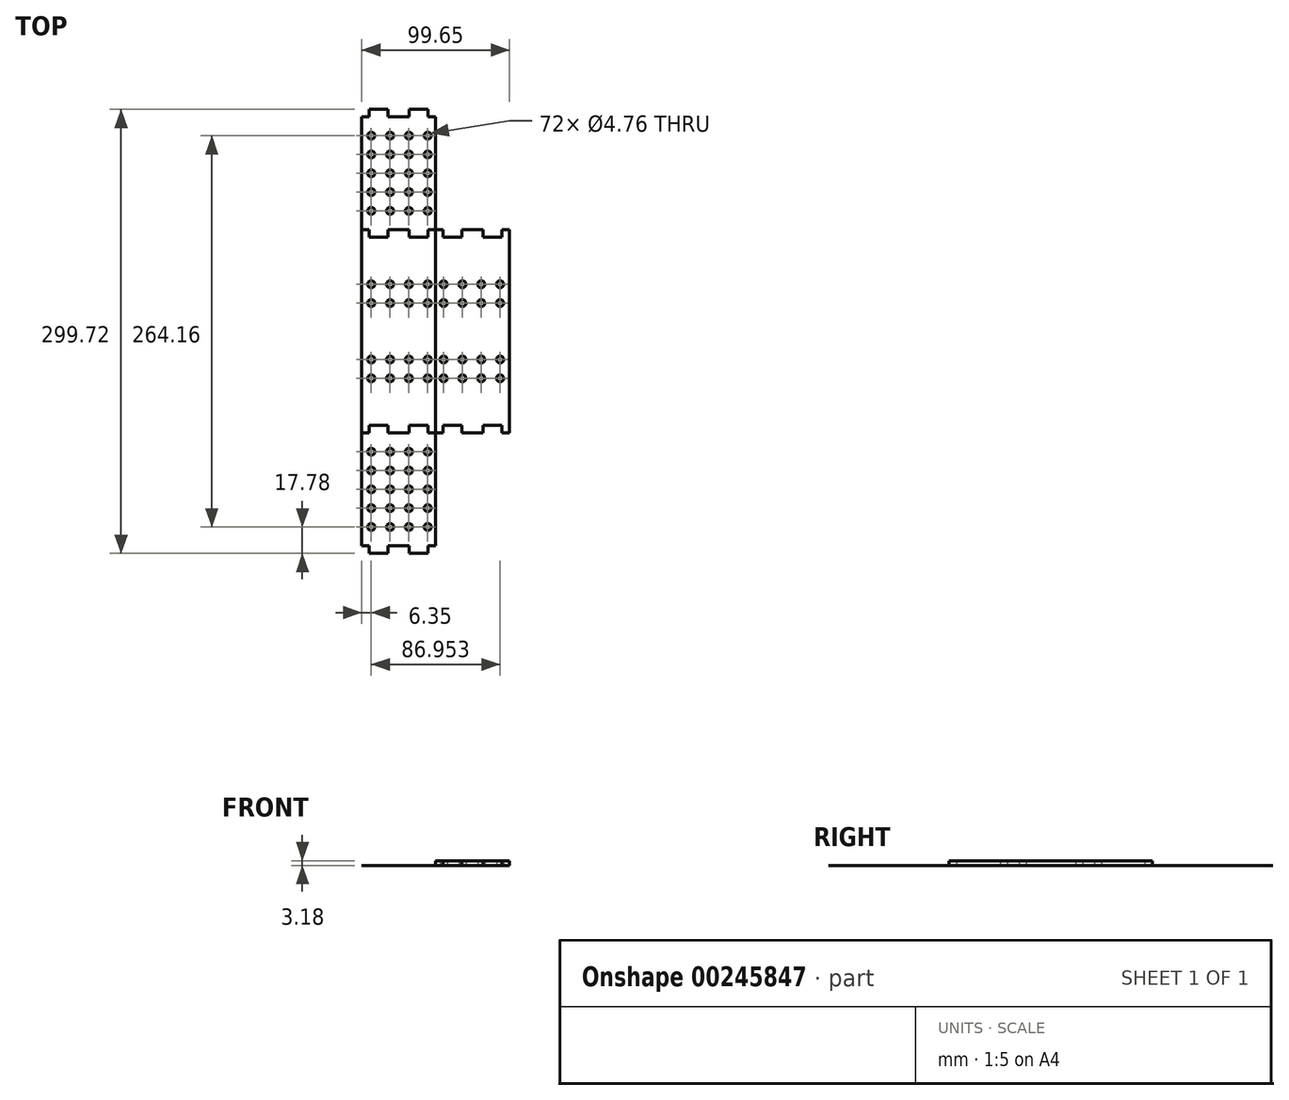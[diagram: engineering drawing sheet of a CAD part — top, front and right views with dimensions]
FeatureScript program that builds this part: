
annotation { "Feature Type Name" : "Feature", "Feature Type Description" : "" }
export const myFeature = defineFeature(function(context is Context, id is Id, definition is map)
    precondition{}
    {
        {
            var Q0;
            Q0=qCreatedBy(makeId("Top.planeOp"),FACE);
            var sketch = newSketch(context, id + "F0", { "sketchPlane" : qUnion([Q0])});
            skLineSegment(sketch, "E0.bottom", {"start": v(-123.2, 27.94) * mm, "end": v(-123.19, 27.94) * mm});
            skLineSegment(sketch, "E0.top", {"start": v(-123.19, -27.94) * mm, "end": v(-123.19, -27.94) * mm});
            skCircle(sketch, "E1.1.0.0", {"center": v(-25.4, -31.75) * mm, "radius": 2.38 * mm});
            skCircle(sketch, "E1.1.1.0", {"center": v(-25.4, -19.05) * mm, "radius": 2.38 * mm});
            skCircle(sketch, "E1.2.0.0", {"center": v(-12.7, -31.75) * mm, "radius": 2.38 * mm});
            skCircle(sketch, "E1.2.1.0", {"center": v(-12.7, -19.05) * mm, "radius": 2.38 * mm});
            skCircle(sketch, "E1.3.0.0", {"center": v(0, -31.75) * mm, "radius": 2.38 * mm});
            skCircle(sketch, "E1.3.1.0", {"center": v(0, -19.05) * mm, "radius": 2.38 * mm});
            skCircle(sketch, "E1.4.0.0", {"center": v(12.7, -31.75) * mm, "radius": 2.38 * mm});
            skCircle(sketch, "E1.4.1.0", {"center": v(12.7, -19.05) * mm, "radius": 2.38 * mm});
            skCircle(sketch, "E2.MirrorC", {"center": v(-12.7, 19.05) * mm, "radius": 2.38 * mm});
            skCircle(sketch, "E3.MirrorC", {"center": v(0, 31.75) * mm, "radius": 2.38 * mm});
            skCircle(sketch, "E4.MirrorC", {"center": v(-25.4, 31.75) * mm, "radius": 2.38 * mm});
            skCircle(sketch, "E5.MirrorC", {"center": v(12.7, 19.05) * mm, "radius": 2.38 * mm});
            skCircle(sketch, "E6.MirrorC", {"center": v(0, 19.05) * mm, "radius": 2.38 * mm});
            skCircle(sketch, "E7.MirrorC", {"center": v(-25.4, 19.05) * mm, "radius": 2.38 * mm});
            skCircle(sketch, "E8.MirrorC", {"center": v(-12.7, 31.75) * mm, "radius": 2.38 * mm});
            skCircle(sketch, "E9.MirrorC", {"center": v(12.7, 31.75) * mm, "radius": 2.38 * mm});
            skLineSegment(sketch, "E10", {"start": v(-31.75, 38.1) * mm, "end": v(-31.75, -38.1) * mm});
            skPoint(sketch, "E10.startSnap0", {"position": v(-31.75, 31.75) * mm});
            skPoint(sketch, "E11.startSnap0", {"position": v(18.08, 31.75) * mm});
            skLineSegment(sketch, "E12", {"start": v(18.08, 38.1) * mm, "end": v(18.08, -38.1) * mm});
            skLineSegment(sketch, "E13.top", {"start": v(-31.75, 68.58) * mm, "end": v(-26.67, 68.58) * mm});
            skLineSegment(sketch, "E13.left", {"start": v(-31.75, 38.1) * mm, "end": v(-31.75, 68.58) * mm});
            skLineSegment(sketch, "E13.right", {"start": v(18.08, 38.1) * mm, "end": v(18.08, 68.58) * mm});
            skLineSegment(sketch, "E14", {"start": v(-26.67, 68.58) * mm, "end": v(-26.67, 63.5) * mm});
            skLineSegment(sketch, "E15", {"start": v(-26.67, 63.5) * mm, "end": v(-13.97, 63.5) * mm});
            skLineSegment(sketch, "E16", {"start": v(-13.97, 63.5) * mm, "end": v(-13.97, 68.58) * mm});
            skLineSegment(sketch, "E17", {"start": v(0.3, 68.58) * mm, "end": v(0.3, 63.5) * mm});
            skLineSegment(sketch, "E18", {"start": v(0.3, 63.5) * mm, "end": v(13, 63.5) * mm});
            skLineSegment(sketch, "E19", {"start": v(13, 63.5) * mm, "end": v(13, 68.58) * mm});
            skLineSegment(sketch, "E20.left", {"start": v(-31.75, 68.58) * mm, "end": v(-31.75, 144.78) * mm});
            skLineSegment(sketch, "E20.right", {"start": v(18.08, 68.58) * mm, "end": v(18.08, 144.78) * mm});
            skLineSegment(sketch, "E21.trimOffspring", {"start": v(-13.97, 68.58) * mm, "end": v(0.3, 68.58) * mm});
            skLineSegment(sketch, "E22.trimOffspring", {"start": v(13, 68.58) * mm, "end": v(18.08, 68.58) * mm});
            skCircle(sketch, "E23.MirrorC", {"center": v(-25.4, 81.28) * mm, "radius": 2.38 * mm});
            skCircle(sketch, "E24.0.1.0", {"center": v(-25.4, 93.98) * mm, "radius": 2.38 * mm});
            skCircle(sketch, "E24.0.2.0", {"center": v(-25.4, 106.68) * mm, "radius": 2.38 * mm});
            skCircle(sketch, "E24.0.3.0", {"center": v(-25.4, 119.38) * mm, "radius": 2.38 * mm});
            skCircle(sketch, "E24.0.4.0", {"center": v(-25.4, 132.08) * mm, "radius": 2.38 * mm});
            skCircle(sketch, "E24.1.0.0", {"center": v(-12.7, 81.28) * mm, "radius": 2.38 * mm});
            skCircle(sketch, "E24.1.1.0", {"center": v(-12.7, 93.98) * mm, "radius": 2.38 * mm});
            skCircle(sketch, "E24.1.2.0", {"center": v(-12.7, 106.68) * mm, "radius": 2.38 * mm});
            skCircle(sketch, "E24.1.3.0", {"center": v(-12.7, 119.38) * mm, "radius": 2.38 * mm});
            skCircle(sketch, "E24.1.4.0", {"center": v(-12.7, 132.08) * mm, "radius": 2.38 * mm});
            skCircle(sketch, "E24.2.0.0", {"center": v(0, 81.28) * mm, "radius": 2.38 * mm});
            skCircle(sketch, "E24.2.1.0", {"center": v(0, 93.98) * mm, "radius": 2.38 * mm});
            skCircle(sketch, "E24.2.2.0", {"center": v(0, 106.68) * mm, "radius": 2.38 * mm});
            skCircle(sketch, "E24.2.3.0", {"center": v(0, 119.38) * mm, "radius": 2.38 * mm});
            skCircle(sketch, "E24.2.4.0", {"center": v(0, 132.08) * mm, "radius": 2.38 * mm});
            skCircle(sketch, "E24.3.0.0", {"center": v(12.7, 81.28) * mm, "radius": 2.38 * mm});
            skCircle(sketch, "E24.3.1.0", {"center": v(12.7, 93.98) * mm, "radius": 2.38 * mm});
            skCircle(sketch, "E24.3.2.0", {"center": v(12.7, 106.68) * mm, "radius": 2.38 * mm});
            skCircle(sketch, "E24.3.3.0", {"center": v(12.7, 119.38) * mm, "radius": 2.38 * mm});
            skCircle(sketch, "E24.3.4.0", {"center": v(12.7, 132.08) * mm, "radius": 2.38 * mm});
            skLineSegment(sketch, "E24.direction1", {"start": v(-25.4, 81.28) * mm, "end": v(-12.7, 81.28) * mm, "construction": true});
            skLineSegment(sketch, "E24.direction2", {"start": v(-25.4, 81.28) * mm, "end": v(-25.4, 93.98) * mm, "construction": true});
            skLineSegment(sketch, "E25", {"start": v(-31.75, 0) * mm, "end": v(18.08, 0) * mm, "construction": true});
            skLineSegment(sketch, "E26.MirrorCS", {"start": v(0.3, -68.58) * mm, "end": v(0.3, -63.5) * mm});
            skCircle(sketch, "E27.MirrorC", {"center": v(0, -106.68) * mm, "radius": 2.38 * mm});
            skLineSegment(sketch, "E28.MirrorCS", {"start": v(13, -68.58) * mm, "end": v(18.08, -68.58) * mm});
            skCircle(sketch, "E29.MirrorC", {"center": v(12.7, -119.38) * mm, "radius": 2.38 * mm});
            skLineSegment(sketch, "E30.MirrorCS", {"start": v(-31.75, -38.1) * mm, "end": v(-31.75, -68.58) * mm});
            skCircle(sketch, "E31.MirrorC", {"center": v(-25.4, -132.08) * mm, "radius": 2.38 * mm});
            skLineSegment(sketch, "E32.MirrorCS", {"start": v(0.3, -63.5) * mm, "end": v(13, -63.5) * mm});
            skCircle(sketch, "E33.MirrorC", {"center": v(0, -119.38) * mm, "radius": 2.38 * mm});
            skLineSegment(sketch, "E34.MirrorCS", {"start": v(-13.97, -68.58) * mm, "end": v(0.3, -68.58) * mm});
            skCircle(sketch, "E35.MirrorC", {"center": v(12.7, -132.08) * mm, "radius": 2.38 * mm});
            skLineSegment(sketch, "E36.MirrorCS", {"start": v(18.08, -38.1) * mm, "end": v(18.08, -68.58) * mm});
            skCircle(sketch, "E37.MirrorC", {"center": v(-12.7, -81.28) * mm, "radius": 2.38 * mm});
            skCircle(sketch, "E38.MirrorC", {"center": v(0, -132.08) * mm, "radius": 2.38 * mm});
            skLineSegment(sketch, "E39.MirrorCS", {"start": v(13, -63.5) * mm, "end": v(13, -68.58) * mm});
            skLineSegment(sketch, "E40.MirrorCS", {"start": v(-31.75, -68.58) * mm, "end": v(-26.67, -68.58) * mm});
            skCircle(sketch, "E41.MirrorC", {"center": v(-25.4, -81.28) * mm, "radius": 2.38 * mm});
            skLineSegment(sketch, "E42.MirrorCS", {"start": v(-25.4, -81.28) * mm, "end": v(-12.7, -81.28) * mm, "construction": true});
            skCircle(sketch, "E43.MirrorC", {"center": v(-12.7, -93.98) * mm, "radius": 2.38 * mm});
            skCircle(sketch, "E44.MirrorC", {"center": v(12.7, -81.28) * mm, "radius": 2.38 * mm});
            skCircle(sketch, "E45.MirrorC", {"center": v(-25.4, -93.98) * mm, "radius": 2.38 * mm});
            skLineSegment(sketch, "E46.MirrorCS", {"start": v(-25.4, -81.28) * mm, "end": v(-25.4, -93.98) * mm, "construction": true});
            skCircle(sketch, "E47.MirrorC", {"center": v(-12.7, -106.68) * mm, "radius": 2.38 * mm});
            skCircle(sketch, "E48.MirrorC", {"center": v(-12.7, -119.38) * mm, "radius": 2.38 * mm});
            skLineSegment(sketch, "E49.MirrorCS", {"start": v(-31.75, -68.58) * mm, "end": v(-31.75, -144.78) * mm});
            skCircle(sketch, "E50.MirrorC", {"center": v(12.7, -93.98) * mm, "radius": 2.38 * mm});
            skLineSegment(sketch, "E51.MirrorCS", {"start": v(-26.67, -68.58) * mm, "end": v(-26.67, -63.5) * mm});
            skLineSegment(sketch, "E52.MirrorCS", {"start": v(18.08, -68.58) * mm, "end": v(18.08, -144.78) * mm});
            skCircle(sketch, "E53.MirrorC", {"center": v(-12.7, -132.08) * mm, "radius": 2.38 * mm});
            skCircle(sketch, "E54.MirrorC", {"center": v(12.7, -106.68) * mm, "radius": 2.38 * mm});
            skLineSegment(sketch, "E55.MirrorCS", {"start": v(-26.67, -63.5) * mm, "end": v(-13.97, -63.5) * mm});
            skCircle(sketch, "E56.MirrorC", {"center": v(0, -81.28) * mm, "radius": 2.38 * mm});
            skCircle(sketch, "E57.MirrorC", {"center": v(-25.4, -106.68) * mm, "radius": 2.38 * mm});
            skLineSegment(sketch, "E58.MirrorCS", {"start": v(-13.97, -63.5) * mm, "end": v(-13.97, -68.58) * mm});
            skCircle(sketch, "E59.MirrorC", {"center": v(0, -93.98) * mm, "radius": 2.38 * mm});
            skCircle(sketch, "E60.MirrorC", {"center": v(-25.4, -119.38) * mm, "radius": 2.38 * mm});
            skLineSegment(sketch, "E61", {"start": v(18.08, 106.68) * mm, "end": v(-31.75, 106.68) * mm, "construction": true});
            skLineSegment(sketch, "E62.MirrorCS", {"start": v(0.3, 149.86) * mm, "end": v(13, 149.86) * mm});
            skLineSegment(sketch, "E63.MirrorCS", {"start": v(13, 149.86) * mm, "end": v(13, 144.78) * mm});
            skLineSegment(sketch, "E64.MirrorCS", {"start": v(-26.67, 144.78) * mm, "end": v(-26.67, 149.86) * mm});
            skLineSegment(sketch, "E65.MirrorCS", {"start": v(-13.97, 149.86) * mm, "end": v(-13.97, 144.78) * mm});
            skLineSegment(sketch, "E66.MirrorCS", {"start": v(13, 144.78) * mm, "end": v(18.08, 144.78) * mm});
            skLineSegment(sketch, "E67.MirrorCS", {"start": v(-31.75, 144.78) * mm, "end": v(-26.67, 144.78) * mm});
            skLineSegment(sketch, "E68.MirrorCS", {"start": v(-26.67, 149.86) * mm, "end": v(-13.97, 149.86) * mm});
            skLineSegment(sketch, "E69.MirrorCS", {"start": v(0.3, 144.78) * mm, "end": v(0.3, 149.86) * mm});
            skLineSegment(sketch, "E70.MirrorCS", {"start": v(-13.97, 144.78) * mm, "end": v(0.3, 144.78) * mm});
            skLineSegment(sketch, "E71", {"start": v(18.08, -106.68) * mm, "end": v(-31.75, -106.68) * mm, "construction": true});
            skLineSegment(sketch, "E72.MirrorCS", {"start": v(-31.75, -144.78) * mm, "end": v(-26.67, -144.78) * mm});
            skLineSegment(sketch, "E73.MirrorCS", {"start": v(-26.67, -144.78) * mm, "end": v(-26.67, -149.86) * mm});
            skLineSegment(sketch, "E74.MirrorCS", {"start": v(-26.67, -149.86) * mm, "end": v(-13.97, -149.86) * mm});
            skLineSegment(sketch, "E75.MirrorCS", {"start": v(-13.97, -149.86) * mm, "end": v(-13.97, -144.78) * mm});
            skLineSegment(sketch, "E76.MirrorCS", {"start": v(-13.97, -144.78) * mm, "end": v(0.3, -144.78) * mm});
            skLineSegment(sketch, "E77.MirrorCS", {"start": v(0.3, -144.78) * mm, "end": v(0.3, -149.86) * mm});
            skLineSegment(sketch, "E78.MirrorCS", {"start": v(0.3, -149.86) * mm, "end": v(13, -149.86) * mm});
            skLineSegment(sketch, "E79.MirrorCS", {"start": v(13, -144.78) * mm, "end": v(18.08, -144.78) * mm});
            skLineSegment(sketch, "E80.MirrorCS", {"start": v(13, -149.86) * mm, "end": v(13, -144.78) * mm});
            skLineSegment(sketch, "E81.MirrorCS", {"start": v(35.86, 63.5) * mm, "end": v(23.16, 63.5) * mm});
            skLineSegment(sketch, "E82.MirrorCS", {"start": v(23.16, 68.58) * mm, "end": v(18.08, 68.58) * mm});
            skCircle(sketch, "E83.MirrorC", {"center": v(23.45, -31.75) * mm, "radius": 2.38 * mm});
            skLineSegment(sketch, "E84.MirrorCS", {"start": v(50.12, -68.58) * mm, "end": v(35.86, -68.58) * mm});
            skLineSegment(sketch, "E85.MirrorCS", {"start": v(62.82, 68.58) * mm, "end": v(62.82, 63.5) * mm});
            skCircle(sketch, "E86.MirrorC", {"center": v(36.15, 19.05) * mm, "radius": 2.38 * mm});
            skLineSegment(sketch, "E87.MirrorCS", {"start": v(35.86, -68.58) * mm, "end": v(35.86, -63.5) * mm});
            skLineSegment(sketch, "E88.MirrorCS", {"start": v(23.16, -68.58) * mm, "end": v(18.08, -68.58) * mm});
            skCircle(sketch, "E89.MirrorC", {"center": v(61.55, -31.75) * mm, "radius": 2.38 * mm});
            skLineSegment(sketch, "E90.MirrorCS", {"start": v(67.9, -38.1) * mm, "end": v(67.9, -68.58) * mm});
            skLineSegment(sketch, "E91.MirrorCS", {"start": v(67.9, 68.58) * mm, "end": v(62.82, 68.58) * mm});
            skLineSegment(sketch, "E92.MirrorCS", {"start": v(67.9, -68.58) * mm, "end": v(62.82, -68.58) * mm});
            skCircle(sketch, "E93.MirrorC", {"center": v(61.55, -19.05) * mm, "radius": 2.38 * mm});
            skCircle(sketch, "E94.MirrorC", {"center": v(23.45, -19.05) * mm, "radius": 2.38 * mm});
            skLineSegment(sketch, "E95.MirrorCS", {"start": v(35.86, 68.58) * mm, "end": v(35.86, 63.5) * mm});
            skLineSegment(sketch, "E96.MirrorCS", {"start": v(35.86, -63.5) * mm, "end": v(23.16, -63.5) * mm});
            skCircle(sketch, "E97.MirrorC", {"center": v(48.85, -31.75) * mm, "radius": 2.38 * mm});
            skLineSegment(sketch, "E98.MirrorCS", {"start": v(62.82, -68.58) * mm, "end": v(62.82, -63.5) * mm});
            skLineSegment(sketch, "E99.MirrorCS", {"start": v(67.9, 0) * mm, "end": v(18.08, 0) * mm, "construction": true});
            skCircle(sketch, "E100.MirrorC", {"center": v(48.85, 19.05) * mm, "radius": 2.38 * mm});
            skCircle(sketch, "E101.MirrorC", {"center": v(61.55, 19.05) * mm, "radius": 2.38 * mm});
            skCircle(sketch, "E102.MirrorC", {"center": v(48.85, -19.05) * mm, "radius": 2.38 * mm});
            skLineSegment(sketch, "E103.MirrorCS", {"start": v(23.16, 63.5) * mm, "end": v(23.16, 68.58) * mm});
            skLineSegment(sketch, "E104.MirrorCS", {"start": v(50.12, 68.58) * mm, "end": v(35.86, 68.58) * mm});
            skCircle(sketch, "E105.MirrorC", {"center": v(36.15, 31.75) * mm, "radius": 2.38 * mm});
            skLineSegment(sketch, "E106.MirrorCS", {"start": v(62.82, 63.5) * mm, "end": v(50.12, 63.5) * mm});
            skCircle(sketch, "E107.MirrorC", {"center": v(48.85, 31.75) * mm, "radius": 2.38 * mm});
            skCircle(sketch, "E108.MirrorC", {"center": v(36.15, -31.75) * mm, "radius": 2.38 * mm});
            skLineSegment(sketch, "E109.MirrorCS", {"start": v(50.12, 63.5) * mm, "end": v(50.12, 68.58) * mm});
            skCircle(sketch, "E110.MirrorC", {"center": v(61.55, 31.75) * mm, "radius": 2.38 * mm});
            skLineSegment(sketch, "E111.MirrorCS", {"start": v(67.9, 38.1) * mm, "end": v(67.9, 68.58) * mm});
            skCircle(sketch, "E112.MirrorC", {"center": v(23.45, 31.75) * mm, "radius": 2.38 * mm});
            skCircle(sketch, "E113.MirrorC", {"center": v(36.15, -19.05) * mm, "radius": 2.38 * mm});
            skLineSegment(sketch, "E114.MirrorCS", {"start": v(23.16, -63.5) * mm, "end": v(23.16, -68.58) * mm});
            skLineSegment(sketch, "E115.MirrorCS", {"start": v(50.12, -63.5) * mm, "end": v(50.12, -68.58) * mm});
            skLineSegment(sketch, "E116.MirrorCS", {"start": v(67.9, 38.1) * mm, "end": v(67.9, -38.1) * mm});
            skPoint(sketch, "E117.MirrorP", {"position": v(67.9, 31.75) * mm});
            skCircle(sketch, "E118.MirrorC", {"center": v(23.45, 19.05) * mm, "radius": 2.38 * mm});
            skLineSegment(sketch, "E119.MirrorCS", {"start": v(62.82, -63.5) * mm, "end": v(50.12, -63.5) * mm});
            skSolve(sketch);
        }
        {
            var Q0;
            Q0=makeQuery(id+"F0.imprint","IMPRINT",FACE,{"disambiguationData":[TD([[makeQuery(id+"F0.imprint","IMPRINT",EDGE,{"derivedFrom":sQuery(id+"F0.wireOp",EDGE,"E81.MirrorCS")}),1.0]])]});
            extrude(context, id + "F1", {"entities" : qUnion([Q0]), "depth" : 3.17 * mm});
        }
        {
            var Q0;
            Q0=makeQuery(id+"F0.imprint","IMPRINT",FACE,{"disambiguationData":[TD([[makeQuery(id+"F0.imprint","IMPRINT",EDGE,{"derivedFrom":sQuery(id+"F0.wireOp",EDGE,"E1.1.0.0")}),-1.0]])]});
            extrude(context, id + "F2", {"entities" : qUnion([Q0]), "depth" : 1 / 203.2 * mm});
        }
        {
            var Q0;
            Q0=makeQuery(id+"F0.imprint","IMPRINT",FACE,{"disambiguationData":[TD([[makeQuery(id+"F0.imprint","IMPRINT",EDGE,{"derivedFrom":sQuery(id+"F0.wireOp",EDGE,"E26.MirrorCS")}),-1.0]])]});
            extrude(context, id + "F3", {"entities" : qUnion([Q0]), "depth" : 1 / 203.2 * mm});
        }
        {
            var Q0;
            Q0=makeQuery(id+"F0.imprint","IMPRINT",FACE,{"disambiguationData":[TD([[makeQuery(id+"F0.imprint","IMPRINT",EDGE,{"derivedFrom":sQuery(id+"F0.wireOp",EDGE,"E14")}),1.0]])]});
            extrude(context, id + "F4", {"entities" : qUnion([Q0]), "depth" : 1 / 203.2 * mm});
        }
    });
